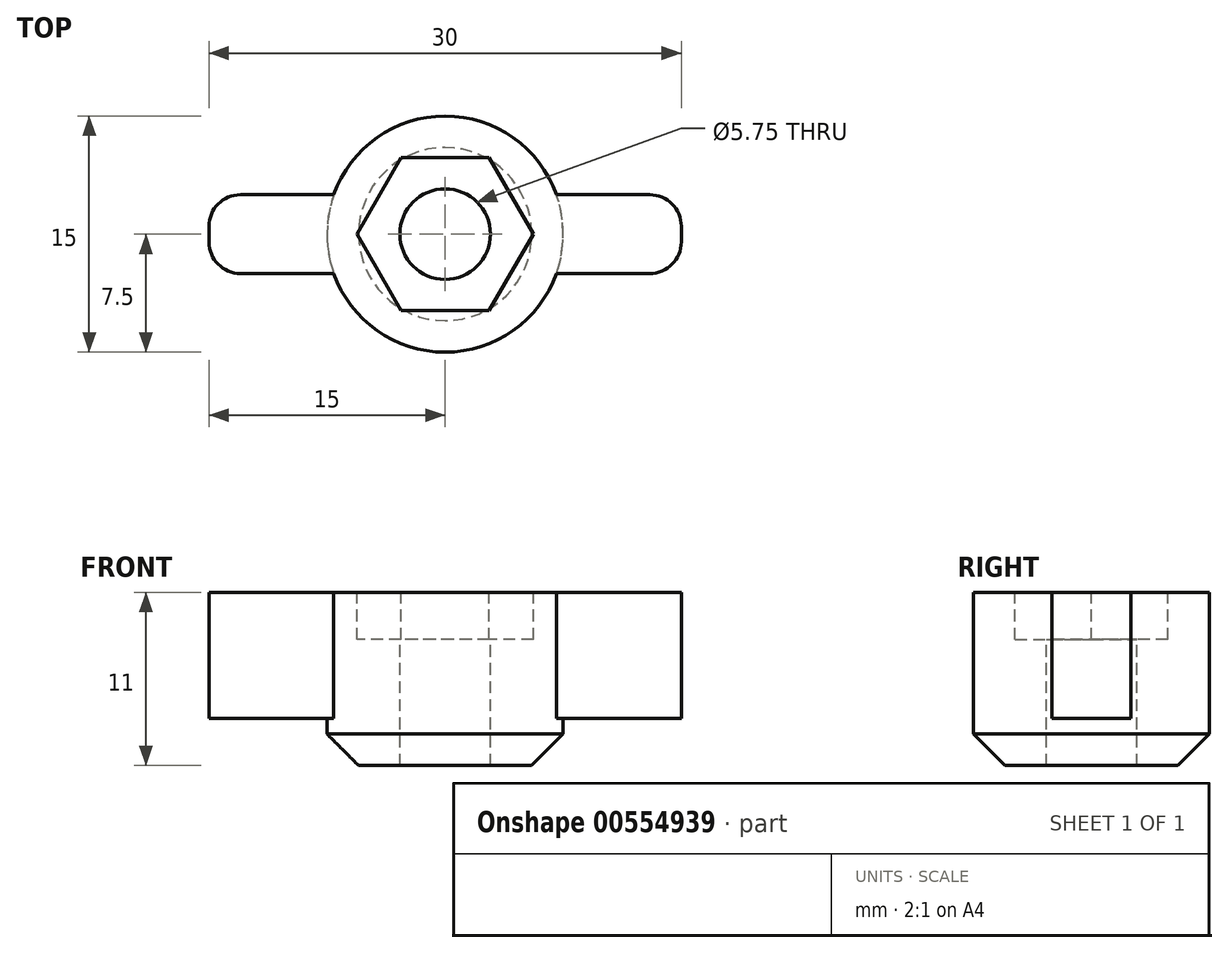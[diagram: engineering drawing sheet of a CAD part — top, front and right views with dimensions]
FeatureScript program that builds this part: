
annotation { "Feature Type Name" : "Feature", "Feature Type Description" : "" }
export const myFeature = defineFeature(function(context is Context, id is Id, definition is map)
    precondition{}
    {
        {
            var Q0;
            Q0=qCreatedBy(makeId("Top.planeOp"),FACE);
            var sketch = newSketch(context, id + "F0", { "sketchPlane" : qUnion([Q0])});
            skCircle(sketch, "E0", {"center": v(0, 0) * mm, "radius": 7.5 * mm});
            skLineSegment(sketch, "E1.bottom", {"start": v(-15, 2.5) * mm, "end": v(15, 2.5) * mm});
            skLineSegment(sketch, "E1.top", {"start": v(-15, -2.5) * mm, "end": v(15, -2.5) * mm});
            skLineSegment(sketch, "E1.left", {"start": v(-15, 2.5) * mm, "end": v(-15, -2.5) * mm});
            skLineSegment(sketch, "E1.right", {"start": v(15, 2.5) * mm, "end": v(15, -2.5) * mm});
            skSolve(sketch);
        }
        {
            var Q0;
            {var subQ5=sQuery(id+"F0.wireOp",EDGE,"E1.left");Q0=makeQuery(id+"F0.imprint","IMPRINT",FACE,{"disambiguationData":[TD([[makeQuery(id+"F0.imprint","IMPRINT",EDGE,{"derivedFrom":subQ5}),1.0]])]});}
            var Q1;
            {var subQ0=sQuery(id+"F0.wireOp",EDGE,"E1.bottom");var subQ1=sQuery(id+"F0.wireOp",EDGE,"E0");var subQ2=makeQuery(id+"F0.imprint","INTERSECT",VERTEX,{"disambiguationData":[OD(0.0)],"derivedFrom":[subQ1,subQ0]});Q1=makeQuery(id+"F0.imprint","IMPRINT",FACE,{"disambiguationData":[TD([[makeQuery(id+"F0.imprint","IMPRINT",EDGE,{"disambiguationData":[TD([[subQ2,-1.0]])],"derivedFrom":subQ1}),1.0]])]});}
            var Q2;
            {var subQ0=sQuery(id+"F0.wireOp",EDGE,"E1.top");var subQ1=sQuery(id+"F0.wireOp",EDGE,"E0");var subQ2=makeQuery(id+"F0.imprint","INTERSECT",VERTEX,{"disambiguationData":[OD(0.0)],"derivedFrom":[subQ1,subQ0]});Q2=makeQuery(id+"F0.imprint","IMPRINT",FACE,{"disambiguationData":[TD([[makeQuery(id+"F0.imprint","IMPRINT",EDGE,{"disambiguationData":[TD([[subQ2,-1.0]])],"derivedFrom":subQ1}),1.0]])]});}
            var Q3;
            {var subQ0=sQuery(id+"F0.wireOp",EDGE,"E1.bottom");var subQ1=sQuery(id+"F0.wireOp",EDGE,"E0");var subQ2=makeQuery(id+"F0.imprint","INTERSECT",VERTEX,{"disambiguationData":[OD(0.0)],"derivedFrom":[subQ1,subQ0]});Q3=makeQuery(id+"F0.imprint","IMPRINT",FACE,{"disambiguationData":[TD([[makeQuery(id+"F0.imprint","IMPRINT",EDGE,{"disambiguationData":[TD([[subQ2,1.0]])],"derivedFrom":subQ1}),1.0]])]});}
            var Q4;
            {var subQ5=sQuery(id+"F0.wireOp",EDGE,"E1.right");Q4=makeQuery(id+"F0.imprint","IMPRINT",FACE,{"disambiguationData":[TD([[makeQuery(id+"F0.imprint","IMPRINT",EDGE,{"derivedFrom":subQ5}),-1.0]])]});}
            extrude(context, id + "F1", {"entities" : qUnion([Q0, Q1, Q2, Q3, Q4]), "depth" : 8 * mm, "offsetDistance" : 25 * mm});
        }
        {
            var Q0;
            Q0=makeQuery(id+"F1.opExtrude","SWEPT_EDGE",EDGE,{"disambiguationData":[OSD([sQuery(id+"F0.wireOp",EDGE,"E1.bottom"),sQuery(id+"F0.wireOp",EDGE,"E1.left")])]});
            var Q1;
            Q1=makeQuery(id+"F1.opExtrude","SWEPT_EDGE",EDGE,{"disambiguationData":[OSD([sQuery(id+"F0.wireOp",EDGE,"E1.top"),sQuery(id+"F0.wireOp",EDGE,"E1.left")])]});
            var Q2;
            Q2=makeQuery(id+"F1.opExtrude","SWEPT_EDGE",EDGE,{"disambiguationData":[OSD([sQuery(id+"F0.wireOp",EDGE,"E1.top"),sQuery(id+"F0.wireOp",EDGE,"E1.right")])]});
            var Q3;
            Q3=makeQuery(id+"F1.opExtrude","SWEPT_EDGE",EDGE,{"disambiguationData":[OSD([sQuery(id+"F0.wireOp",EDGE,"E1.bottom"),sQuery(id+"F0.wireOp",EDGE,"E1.right")])]});
            fillet(context, id + "F2", {"entities" : qUnion([Q0, Q1, Q2, Q3]), "radius" : 2 * mm, "tangentPropagation" : true, "allowEdgeOverflow" : false});
        }
        {
            var Q0;
            Q0=makeQuery(id+"F1.opExtrude","CAP_FACE",FACE,{"disambiguationData":[OSD([sQuery(id+"F0.wireOp",EDGE,"E0"),sQuery(id+"F0.wireOp",EDGE,"E1.bottom"),sQuery(id+"F0.wireOp",EDGE,"E1.top"),sQuery(id+"F0.wireOp",EDGE,"E1.left"),sQuery(id+"F0.wireOp",EDGE,"E1.right")])],"isStart":false});
            var sketch = newSketch(context, id + "F3", { "sketchPlane" : qUnion([Q0])});
            skCircle(sketch, "E2", {"center": v(0, 0) * mm, "radius": 2.88 * mm});
            skSolve(sketch);
        }
        {
            var Q0;
            Q0=makeQuery(id+"F3.imprint","IMPRINT",FACE,{"disambiguationData":[TD([[makeQuery(id+"F3.imprint","IMPRINT",EDGE,{"derivedFrom":sQuery(id+"F3.wireOp",EDGE,"E2")}),1.0]])]});
            extrude(context, id + "F4", {"entities" : qUnion([Q0]), "operationType" : NewBodyOperationType.REMOVE, "endBound" : BoundingType.THROUGH_ALL, "oppositeDirection" : true, "depth" : 25 * mm, "offsetDistance" : 25 * mm});
        }
        {
            var Q0;
            Q0=makeQuery(id+"F1.opExtrude","CAP_FACE",FACE,{"disambiguationData":[OSD([sQuery(id+"F0.wireOp",EDGE,"E0"),sQuery(id+"F0.wireOp",EDGE,"E1.bottom"),sQuery(id+"F0.wireOp",EDGE,"E1.top"),sQuery(id+"F0.wireOp",EDGE,"E1.left"),sQuery(id+"F0.wireOp",EDGE,"E1.right")])],"isStart":false});
            var sketch = newSketch(context, id + "F5", { "sketchPlane" : qUnion([Q0])});
            skCircle(sketch, "E3.cCircle", {"center": v(0, 0) * mm, "radius": 4.85 * mm, "construction": true});
            skLineSegment(sketch, "E3.0", {"start": v(-2.8, -4.85) * mm, "end": v(-5.6, 0) * mm});
            skLineSegment(sketch, "E3.1", {"start": v(-5.6, 0) * mm, "end": v(-2.8, 4.85) * mm});
            skLineSegment(sketch, "E3.2", {"start": v(-2.8, 4.85) * mm, "end": v(2.8, 4.85) * mm});
            skLineSegment(sketch, "E3.3", {"start": v(2.8, 4.85) * mm, "end": v(5.6, 0) * mm});
            skLineSegment(sketch, "E3.4", {"start": v(5.6, 0) * mm, "end": v(2.8, -4.85) * mm});
            skLineSegment(sketch, "E3.5", {"start": v(2.8, -4.85) * mm, "end": v(-2.8, -4.85) * mm});
            skPoint(sketch, "E3.0.midPoint", {"position": v(-4.2, -2.42) * mm});
            skSolve(sketch);
        }
        {
            var Q0;
            Q0=makeQuery(id+"F5.imprint","IMPRINT",FACE,{"disambiguationData":[TD([[makeQuery(id+"F5.imprint","IMPRINT",EDGE,{"derivedFrom":sQuery(id+"F5.wireOp",EDGE,"E3.0")}),-1.0]])]});
            extrude(context, id + "F6", {"entities" : qUnion([Q0]), "operationType" : NewBodyOperationType.REMOVE, "oppositeDirection" : true, "depth" : 3 * mm, "offsetDistance" : 25 * mm});
        }
        {
            var Q0;
            Q0=makeQuery(id+"F1.opExtrude","CAP_FACE",FACE,{"disambiguationData":[OSD([sQuery(id+"F0.wireOp",EDGE,"E0"),sQuery(id+"F0.wireOp",EDGE,"E1.bottom"),sQuery(id+"F0.wireOp",EDGE,"E1.top"),sQuery(id+"F0.wireOp",EDGE,"E1.left"),sQuery(id+"F0.wireOp",EDGE,"E1.right")])],"isStart":true});
            var sketch = newSketch(context, id + "F7", { "sketchPlane" : qUnion([Q0])});
            skCircle(sketch, "E4", {"center": v(0, 0) * mm, "radius": 7.5 * mm});
            skSolve(sketch);
        }
        {
            var Q0;
            {var subQ1=sQuery(id+"F0.wireOp",EDGE,"E1.right");var subQ2=sQuery(id+"F0.wireOp",EDGE,"E1.bottom");var subQ3=sQuery(id+"F0.wireOp",EDGE,"E0");var subQ5=sQuery(id+"F0.wireOp",EDGE,"E1.top");var subQ7=sQuery(id+"F0.wireOp",EDGE,"E1.left");Q0=makeQuery(id+"F7.imprint","IMPRINT",FACE,{"disambiguationData":[TD([[makeQuery(id+"F7.imprint","IMPRINT",EDGE,{"derivedFrom":makeQuery(id+"F4.boolean.opBoolean","INTERSECT",EDGE,{"derivedFrom":[makeQuery(id+"F1.opExtrude","CAP_FACE",FACE,{"disambiguationData":[OSD([subQ3,subQ2,subQ5,subQ7,subQ1])],"isStart":true}),makeQuery(id+"F4.opExtrude","SWEPT_FACE",FACE,{"disambiguationData":[OSD([sQuery(id+"F3.wireOp",EDGE,"E2")])]})]})}),1.0]])]});}
            extrude(context, id + "F8", {"entities" : qUnion([Q0]), "operationType" : NewBodyOperationType.ADD, "depth" : 3 * mm, "offsetDistance" : 25 * mm});
        }
        {
            var Q0;
            Q0=makeQuery(id+"F8.opExtrude","CAP_EDGE",EDGE,{"disambiguationData":[OSD([sQuery(id+"F7.wireOp",EDGE,"E4")])],"isStart":false});
            chamfer(context, id + "F9", {"entities" : qUnion([Q0]), "width" : 2 * mm, "tangentPropagation" : true});
        }
    });
